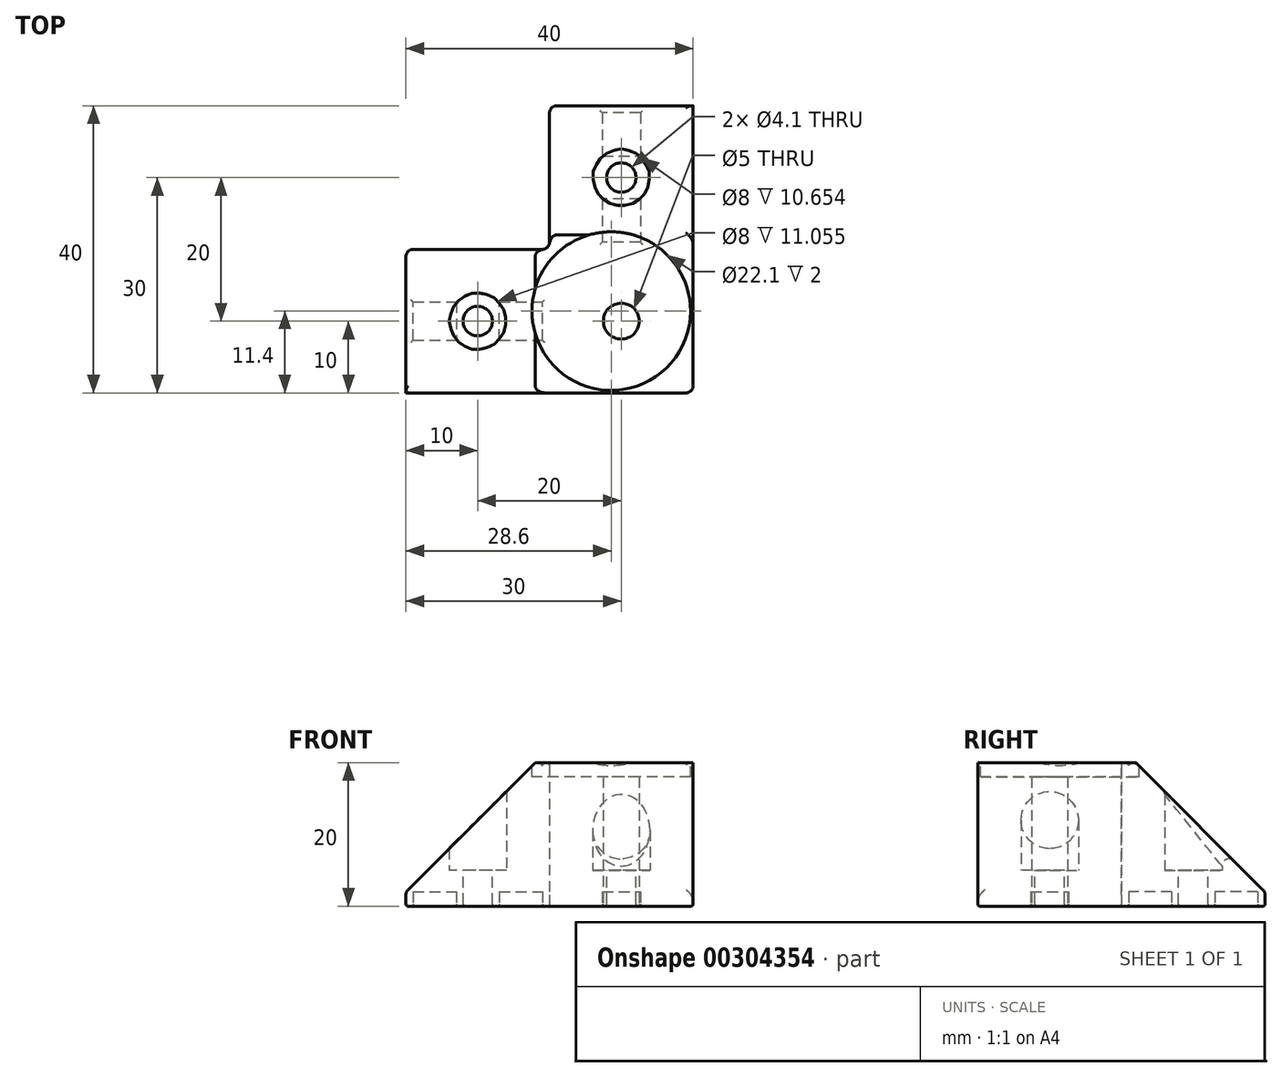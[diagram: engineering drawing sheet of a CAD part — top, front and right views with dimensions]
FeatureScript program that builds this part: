
annotation { "Feature Type Name" : "Feature", "Feature Type Description" : "" }
export const myFeature = defineFeature(function(context is Context, id is Id, definition is map)
    precondition{}
    {
        {
            var Q0;
            Q0=qCreatedBy(makeId("Top.planeOp"),FACE);
            var sketch = newSketch(context, id + "F0", { "sketchPlane" : qUnion([Q0])});
            skLineSegment(sketch, "E0", {"start": v(0, 0) * mm, "end": v(0, 40) * mm});
            skLineSegment(sketch, "E1", {"start": v(0, 40) * mm, "end": v(-20, 40) * mm});
            skLineSegment(sketch, "E2", {"start": v(-20, 40) * mm, "end": v(-20, 20) * mm});
            skLineSegment(sketch, "E3", {"start": v(-20, 20) * mm, "end": v(-40, 20) * mm});
            skLineSegment(sketch, "E4", {"start": v(-40, 20) * mm, "end": v(-40, 0) * mm});
            skLineSegment(sketch, "E5", {"start": v(-40, 0) * mm, "end": v(0, 0) * mm});
            skSolve(sketch);
        }
        {
            var Q0;
            Q0=makeQuery(id+"F0.imprint","IMPRINT",FACE,{"disambiguationData":[TD([[makeQuery(id+"F0.imprint","IMPRINT",EDGE,{"derivedFrom":sQuery(id+"F0.wireOp",EDGE,"E0")}),1.0]])]});
            extrude(context, id + "F1", {"entities" : qUnion([Q0]), "depth" : 20 * mm});
        }
        {
            var Q0;
            Q0=makeQuery(id+"F1.opExtrude","CAP_EDGE",EDGE,{"disambiguationData":[OSD([sQuery(id+"F0.wireOp",EDGE,"E4")])],"isStart":false});
            var Q1;
            Q1=makeQuery(id+"F1.opExtrude","CAP_EDGE",EDGE,{"disambiguationData":[OSD([sQuery(id+"F0.wireOp",EDGE,"E1")])],"isStart":false});
            chamfer(context, id + "F2", {"entities" : qUnion([Q0, Q1]), "width" : 18 * mm, "tangentPropagation" : true});
        }
        {
            var Q0;
            Q0=qCreatedBy(makeId("Top.planeOp"),FACE);
            cPlane(context, id + "F3", {"entities" : qUnion([Q0]), "cplaneType" : CPlaneType.OFFSET, "offset" : 5 * mm, "width" : 150 * mm, "height" : 150 * mm});
        }
        {
            var Q0;
            Q0=qCreatedBy(id+"F3.planeOp",FACE);
            var sketch = newSketch(context, id + "F4", { "sketchPlane" : qUnion([Q0])});
            skCircle(sketch, "E6", {"center": v(-30, 10) * mm, "radius": 4 * mm});
            skLineSegment(sketch, "E7", {"start": v(0, 0) * mm, "end": v(-34.38, 34.38) * mm, "construction": true});
            skCircle(sketch, "E8.MirrorC", {"center": v(-10, 30) * mm, "radius": 4 * mm});
            skSolve(sketch);
        }
        {
            var Q0;
            Q0 = qSketchRegion(id + "F4", true);
            var Q1;
            Q1=makeQuery(id+"F2.opChamfer","BLEND_FACE",FACE,{"disambiguationData":[OSD([sQuery(id+"F0.wireOp",EDGE,"E4")])]});
            extrude(context, id + "F5", {"entities" : qUnion([Q0]), "operationType" : NewBodyOperationType.REMOVE, "endBound" : BoundingType.UP_TO_SURFACE, "endBoundEntityFace" : qUnion([Q1]), "depth" : 25 * mm});
        }
        {
            var Q0;
            Q0=makeQuery(id+"F5.boolean.opBoolean","COPY",FACE,{"derivedFrom":makeQuery(id+"F5.opExtrude","CAP_FACE",FACE,{"disambiguationData":[OSD([sQuery(id+"F4.wireOp",EDGE,"E6")])],"isStart":true})});
            var sketch = newSketch(context, id + "F6", { "sketchPlane" : qUnion([Q0])});
            skCircle(sketch, "E9", {"center": v(-30, 10) * mm, "radius": 2.05 * mm});
            skLineSegment(sketch, "E10", {"start": v(0, 0) * mm, "end": v(-31.94, 31.94) * mm, "construction": true});
            skCircle(sketch, "E11.MirrorC", {"center": v(-10, 30) * mm, "radius": 2.05 * mm});
            skSolve(sketch);
        }
        {
            var Q0;
            Q0 = qSketchRegion(id + "F6", true);
            extrude(context, id + "F7", {"entities" : qUnion([Q0]), "operationType" : NewBodyOperationType.REMOVE, "endBound" : BoundingType.THROUGH_ALL, "oppositeDirection" : true, "depth" : 25 * mm});
        }
        {
            var Q0;
            Q0=qCreatedBy(makeId("Top.planeOp"),FACE);
            var sketch = newSketch(context, id + "F8", { "sketchPlane" : qUnion([Q0])});
            skCircle(sketch, "E12", {"center": v(-10, 10) * mm, "radius": 2.5 * mm});
            skSolve(sketch);
        }
        {
            var Q0;
            Q0 = qSketchRegion(id + "F8", true);
            extrude(context, id + "F9", {"entities" : qUnion([Q0]), "operationType" : NewBodyOperationType.REMOVE, "endBound" : BoundingType.THROUGH_ALL, "depth" : 25 * mm});
        }
        {
            var Q0;
            Q0=makeQuery(id+"F1.opExtrude","CAP_FACE",FACE,{"disambiguationData":[OSD([sQuery(id+"F0.wireOp",EDGE,"E0"),sQuery(id+"F0.wireOp",EDGE,"E1"),sQuery(id+"F0.wireOp",EDGE,"E2"),sQuery(id+"F0.wireOp",EDGE,"E3"),sQuery(id+"F0.wireOp",EDGE,"E4"),sQuery(id+"F0.wireOp",EDGE,"E5")])],"isStart":false});
            var sketch = newSketch(context, id + "F10", { "sketchPlane" : qUnion([Q0])});
            skCircle(sketch, "E13", {"center": v(-11.4, 11.4) * mm, "radius": 11.05 * mm});
            skLineSegment(sketch, "E14", {"start": v(-20, 20) * mm, "end": v(0, 0) * mm, "construction": true});
            skSolve(sketch);
        }
        {
            var Q0;
            Q0 = qSketchRegion(id + "F10", true);
            extrude(context, id + "F11", {"entities" : qUnion([Q0]), "operationType" : NewBodyOperationType.REMOVE, "oppositeDirection" : true, "depth" : 2 * mm});
        }
        {
            var Q0;
            Q0=makeQuery(id+"F1.opExtrude","CAP_FACE",FACE,{"disambiguationData":[OSD([sQuery(id+"F0.wireOp",EDGE,"E0"),sQuery(id+"F0.wireOp",EDGE,"E1"),sQuery(id+"F0.wireOp",EDGE,"E2"),sQuery(id+"F0.wireOp",EDGE,"E3"),sQuery(id+"F0.wireOp",EDGE,"E4"),sQuery(id+"F0.wireOp",EDGE,"E5")])],"isStart":true});
            var sketch = newSketch(context, id + "F12", { "sketchPlane" : qUnion([Q0])});
            skLineSegment(sketch, "E15.bottom", {"start": v(-39, -7.35) * mm, "end": v(-33, -7.35) * mm});
            skLineSegment(sketch, "E16", {"start": v(-10, -10) * mm, "end": v(-40, -10) * mm, "construction": true});
            skLineSegment(sketch, "E17", {"start": v(-10, -10) * mm, "end": v(-20, -20) * mm, "construction": true});
            skLineSegment(sketch, "E18.MirrorCS", {"start": v(-39, -12.65) * mm, "end": v(-33, -12.65) * mm});
            skLineSegment(sketch, "E19", {"start": v(-39, -7.35) * mm, "end": v(-39, -12.65) * mm});
            skLineSegment(sketch, "E20", {"start": v(-33, -12.65) * mm, "end": v(-33, -7.35) * mm});
            skLineSegment(sketch, "E21.bottom", {"start": v(-27, -7.35) * mm, "end": v(-21, -7.35) * mm});
            skLineSegment(sketch, "E21.top", {"start": v(-27, -12.65) * mm, "end": v(-21, -12.65) * mm});
            skLineSegment(sketch, "E21.left", {"start": v(-27, -7.35) * mm, "end": v(-27, -12.65) * mm});
            skLineSegment(sketch, "E21.right", {"start": v(-21, -7.35) * mm, "end": v(-21, -12.65) * mm});
            skLineSegment(sketch, "E22.MirrorCS", {"start": v(-12.65, -27) * mm, "end": v(-12.65, -21) * mm});
            skLineSegment(sketch, "E23.MirrorCS", {"start": v(-7.35, -27) * mm, "end": v(-7.35, -21) * mm});
            skLineSegment(sketch, "E24.MirrorCS", {"start": v(-7.35, -21) * mm, "end": v(-12.65, -21) * mm});
            skLineSegment(sketch, "E25.MirrorCS", {"start": v(-7.35, -27) * mm, "end": v(-12.65, -27) * mm});
            skLineSegment(sketch, "E26.MirrorCS", {"start": v(-12.65, -33) * mm, "end": v(-7.35, -33) * mm});
            skLineSegment(sketch, "E27.MirrorCS", {"start": v(-12.65, -39) * mm, "end": v(-12.65, -33) * mm});
            skLineSegment(sketch, "E28.MirrorCS", {"start": v(-7.35, -39) * mm, "end": v(-12.65, -39) * mm});
            skLineSegment(sketch, "E29.MirrorCS", {"start": v(-7.35, -39) * mm, "end": v(-7.35, -33) * mm});
            skSolve(sketch);
        }
        {
            var Q0;
            Q0 = qSketchRegion(id + "F12", true);
            extrude(context, id + "F13", {"entities" : qUnion([Q0]), "operationType" : NewBodyOperationType.REMOVE, "oppositeDirection" : true, "depth" : 2 * mm});
        }
        {
            var Q0;
            Q0=makeQuery(id+"F1.opExtrude","SWEPT_EDGE",EDGE,{"disambiguationData":[OSD([sQuery(id+"F0.wireOp",EDGE,"E0"),sQuery(id+"F0.wireOp",EDGE,"E5")])]});
            var Q1;
            Q1=makeQuery(id+"F2.opChamfer","BLEND_EDGE",EDGE,{"blendedFrom":[makeQuery(id+"F1.opExtrude","CAP_EDGE",EDGE,{"disambiguationData":[OSD([sQuery(id+"F0.wireOp",EDGE,"E1")])],"isStart":false}),makeQuery(id+"F1.opExtrude","SWEPT_FACE",FACE,{"disambiguationData":[OSD([sQuery(id+"F0.wireOp",EDGE,"E0")])]})],"blendedInto":[makeQuery(id+"F1.opExtrude","SWEPT_FACE",FACE,{"disambiguationData":[OSD([sQuery(id+"F0.wireOp",EDGE,"E0")])]})]});
            var Q2;
            Q2=makeQuery(id+"F2.opChamfer","BLEND_EDGE",EDGE,{"blendedFrom":[makeQuery(id+"F1.opExtrude","CAP_EDGE",EDGE,{"disambiguationData":[OSD([sQuery(id+"F0.wireOp",EDGE,"E4")])],"isStart":false}),makeQuery(id+"F1.opExtrude","SWEPT_FACE",FACE,{"disambiguationData":[OSD([sQuery(id+"F0.wireOp",EDGE,"E5")])]})],"blendedInto":[makeQuery(id+"F1.opExtrude","SWEPT_FACE",FACE,{"disambiguationData":[OSD([sQuery(id+"F0.wireOp",EDGE,"E5")])]})]});
            var Q3;
            Q3=makeQuery(id+"F1.opExtrude","SWEPT_EDGE",EDGE,{"disambiguationData":[OSD([sQuery(id+"F0.wireOp",EDGE,"E2"),sQuery(id+"F0.wireOp",EDGE,"E3")])]});
            var Q4;
            Q4=makeQuery(id+"F5.boolean.opBoolean","INTERSECT",EDGE,{"derivedFrom":[makeQuery(id+"F2.opChamfer","BLEND_FACE",FACE,{"disambiguationData":[OSD([sQuery(id+"F0.wireOp",EDGE,"E1")])]}),makeQuery(id+"F5.opExtrude","SWEPT_FACE",FACE,{"disambiguationData":[OSD([sQuery(id+"F4.wireOp",EDGE,"E8.MirrorC")])]})]});
            var Q5;
            Q5=makeQuery(id+"F5.boolean.opBoolean","COPY",EDGE,{"derivedFrom":makeQuery(id+"F5.opExtrude","CAP_EDGE",EDGE,{"disambiguationData":[OSD([sQuery(id+"F4.wireOp",EDGE,"E6")])],"isStart":false})});
            var Q6;
            {var subQ0=sQuery(id+"F0.wireOp",EDGE,"E4");Q6=makeQuery(id+"F2.opChamfer","BLEND_EDGE",EDGE,{"blendedFrom":[makeQuery(id+"F1.opExtrude","CAP_EDGE",EDGE,{"disambiguationData":[OSD([subQ0])],"isStart":false}),makeQuery(id+"F1.opExtrude","SWEPT_FACE",FACE,{"disambiguationData":[OSD([subQ0])]})],"blendedInto":[makeQuery(id+"F1.opExtrude","SWEPT_FACE",FACE,{"disambiguationData":[OSD([subQ0])]})]});}
            var Q7;
            {var subQ0=sQuery(id+"F0.wireOp",EDGE,"E1");Q7=makeQuery(id+"F2.opChamfer","BLEND_EDGE",EDGE,{"blendedFrom":[makeQuery(id+"F1.opExtrude","CAP_EDGE",EDGE,{"disambiguationData":[OSD([subQ0])],"isStart":false}),makeQuery(id+"F1.opExtrude","SWEPT_FACE",FACE,{"disambiguationData":[OSD([subQ0])]})],"blendedInto":[makeQuery(id+"F1.opExtrude","SWEPT_FACE",FACE,{"disambiguationData":[OSD([subQ0])]})]});}
            var Q8;
            {var subQ0=sQuery(id+"F0.wireOp",EDGE,"E0");var subQ1=sQuery(id+"F0.wireOp",EDGE,"E1");var subQ2=makeQuery(id+"F1.opExtrude","CAP_FACE",FACE,{"disambiguationData":[OSD([subQ0,subQ1,sQuery(id+"F0.wireOp",EDGE,"E2"),sQuery(id+"F0.wireOp",EDGE,"E3"),sQuery(id+"F0.wireOp",EDGE,"E4"),sQuery(id+"F0.wireOp",EDGE,"E5")])],"isStart":false});Q8=makeQuery(id+"F11.boolean.opBoolean","SPLIT",EDGE,{"disambiguationData":[TD([makeQuery(id+"F1.opExtrude","SWEPT_FACE",FACE,{"disambiguationData":[OSD([subQ0])]})])],"derivedFrom":makeQuery(id+"F2.opChamfer","BLEND_EDGE",EDGE,{"blendedFrom":[makeQuery(id+"F1.opExtrude","CAP_EDGE",EDGE,{"disambiguationData":[OSD([subQ1])],"isStart":false}),subQ2],"blendedInto":[subQ2]})});}
            fillet(context, id + "F14", {"entities" : qUnion([Q0, Q1, Q2, Q3, Q4, Q5, Q6, Q7, Q8]), "radius" : 1 * mm, "tangentPropagation" : true, "allowEdgeOverflow" : false});
        }
        {
            var Q0;
            Q0=makeQuery(id+"F2.opChamfer","BLEND_EDGE",EDGE,{"blendedFrom":[makeQuery(id+"F1.opExtrude","CAP_EDGE",EDGE,{"disambiguationData":[OSD([sQuery(id+"F0.wireOp",EDGE,"E4")])],"isStart":false}),makeQuery(id+"F1.opExtrude","SWEPT_FACE",FACE,{"disambiguationData":[OSD([sQuery(id+"F0.wireOp",EDGE,"E3")])]})],"blendedInto":[makeQuery(id+"F1.opExtrude","SWEPT_FACE",FACE,{"disambiguationData":[OSD([sQuery(id+"F0.wireOp",EDGE,"E3")])]})]});
            var Q1;
            Q1=makeQuery(id+"F2.opChamfer","BLEND_EDGE",EDGE,{"blendedFrom":[makeQuery(id+"F1.opExtrude","CAP_EDGE",EDGE,{"disambiguationData":[OSD([sQuery(id+"F0.wireOp",EDGE,"E1")])],"isStart":false}),makeQuery(id+"F1.opExtrude","SWEPT_FACE",FACE,{"disambiguationData":[OSD([sQuery(id+"F0.wireOp",EDGE,"E2")])]})],"blendedInto":[makeQuery(id+"F1.opExtrude","SWEPT_FACE",FACE,{"disambiguationData":[OSD([sQuery(id+"F0.wireOp",EDGE,"E2")])]})]});
            fillet(context, id + "F15", {"entities" : qUnion([Q0, Q1]), "radius" : 1 * mm, "tangentPropagation" : true, "allowEdgeOverflow" : false});
        }
        {
            var Q0;
            Q0=makeQuery(id+"F1.opExtrude","CAP_FACE",FACE,{"disambiguationData":[OSD([sQuery(id+"F0.wireOp",EDGE,"E0"),sQuery(id+"F0.wireOp",EDGE,"E1"),sQuery(id+"F0.wireOp",EDGE,"E2"),sQuery(id+"F0.wireOp",EDGE,"E3"),sQuery(id+"F0.wireOp",EDGE,"E4"),sQuery(id+"F0.wireOp",EDGE,"E5")])],"isStart":true});
            fillet(context, id + "F16", {"entities" : qUnion([Q0]), "radius" : 0.3 * mm, "tangentPropagation" : true, "allowEdgeOverflow" : false});
        }
    });
